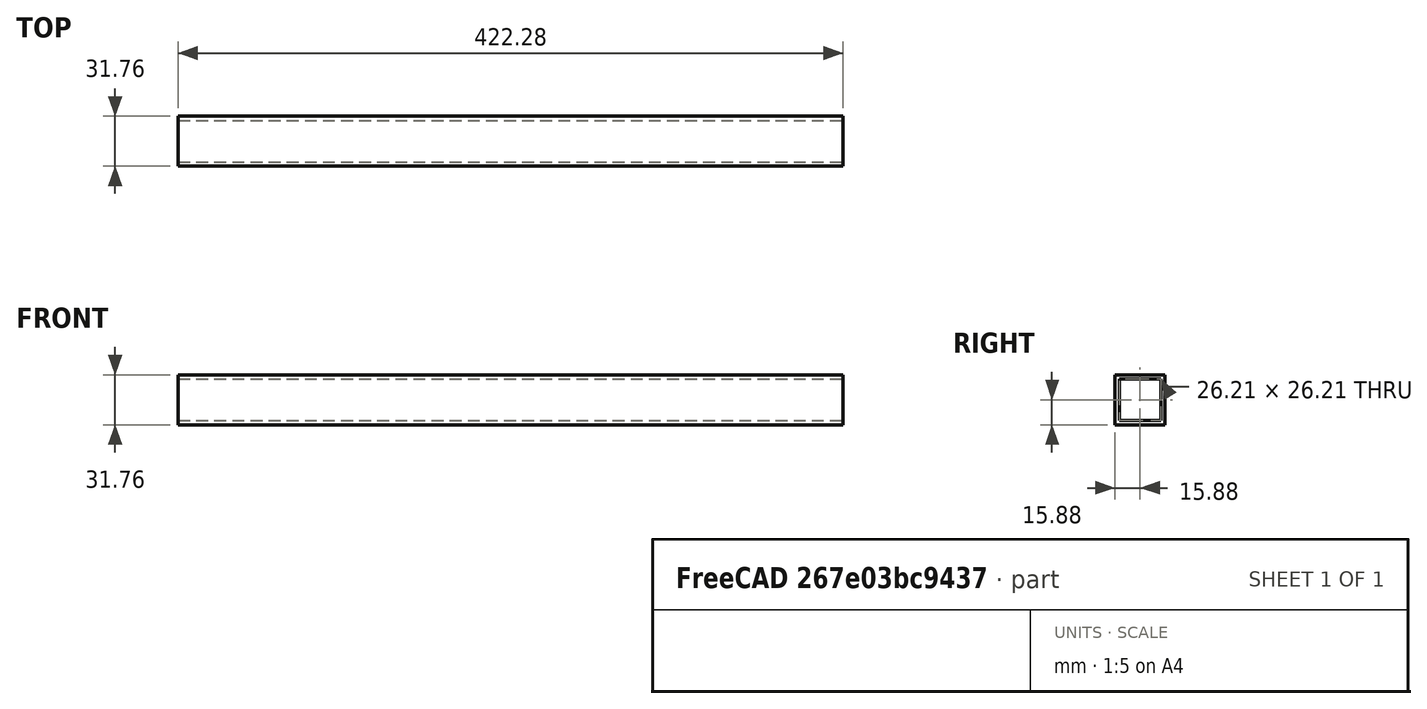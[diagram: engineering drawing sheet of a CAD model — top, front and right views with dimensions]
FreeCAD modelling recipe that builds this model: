
FCSTD DOCUMENT  (FreeCAD 0.16R6062 (Git))
Label: Chassis-Bottom-Part-6
License: All rights reserved
LicenseURL: http://en.wikipedia.org/wiki/All_rights_reserved
objects: Sketcher::SketchObject×1, PartDesign::Pad×1
note: 3 computed .brp shape members not serialized (recipe doc carries the construction recipe); baked Part::Feature solids carry a one-line shape summary decoded from their .brp

FEATURE [Sketcher::SketchObject] Sketch
  Placement = pos=(0,0,0) rot=(0.57735,0.57735,0.57735;2.0944rad)
  sketch-geometry (8):
    g0: LineSegment StartX=-15.875 StartY=15.875 StartZ=0 EndX=15.875 EndY=15.875 EndZ=0
    g1: LineSegment StartX=15.875 StartY=15.875 StartZ=0 EndX=15.875 EndY=-15.875 EndZ=0
    g2: LineSegment StartX=15.875 StartY=-15.875 StartZ=0 EndX=-15.875 EndY=-15.875 EndZ=0
    g3: LineSegment StartX=-15.875 StartY=-15.875 StartZ=0 EndX=-15.875 EndY=15.875 EndZ=0
    g4: LineSegment StartX=-13.1064 StartY=13.1064 StartZ=0 EndX=13.1064 EndY=13.1064 EndZ=0
    g5: LineSegment StartX=13.1064 StartY=13.1064 StartZ=0 EndX=13.1064 EndY=-13.1064 EndZ=0
    g6: LineSegment StartX=13.1064 StartY=-13.1064 StartZ=0 EndX=-13.1064 EndY=-13.1064 EndZ=0
    g7: LineSegment StartX=-13.1064 StartY=-13.1064 StartZ=0 EndX=-13.1064 EndY=13.1064 EndZ=0
  constraints (22):
    c: Coincident(g0,g1)
    c: Coincident(g1,g2)
    c: Coincident(g2,g3)
    c: Coincident(g3,g0)
    c: Horizontal(g0)
    c: Horizontal(g2)
    c: Vertical(g1)
    c: Vertical(g3)
    c: Equal(g2,g1)
    c: DistanceX(g0) = 31.75
    c: Symmetric(g0,g1,g-1)
    c: Coincident(g4,g5)
    c: Coincident(g5,g6)
    c: Coincident(g6,g7)
    c: Coincident(g7,g4)
    c: Horizontal(g4)
    c: Horizontal(g6)
    c: Vertical(g5)
    c: Vertical(g7)
    c: Equal(g6,g5)
    c: DistanceX(g4) = 26.2128
    c: Symmetric(g4,g5,g-1)
FEATURE [PartDesign::Pad] Pad
  Length = 211.137
  Length2 = 211.137
  Placement = pos=(0,0,0) rot=(0.57735,0.57735,0.57735;2.0944rad)
  Sketch = -> Sketch
  Type = 4
